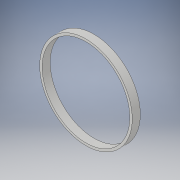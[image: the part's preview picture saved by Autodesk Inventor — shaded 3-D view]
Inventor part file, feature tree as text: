
AUTODESK INVENTOR PART (.ipt)
format: ipt  version: 2019 (Build 230136000, 136)  size: 101,888 bytes
history: native  units: mm
features: extrude x1, sketch x1
ambient origin geometry x8: Origin, YZ Plane, XZ Plane, XY Plane, X Axis, Y Axis, Z Axis, Center Point
bodies: Solid1 (feature_tree)
feature tree (2):
  extrude  "Extrusion1"  Depth=20.0mm
  sketch  "Sketch1"  dims[d0=230.0mm d1=218.0mm d2=20.0mm d3=0.0mm]
